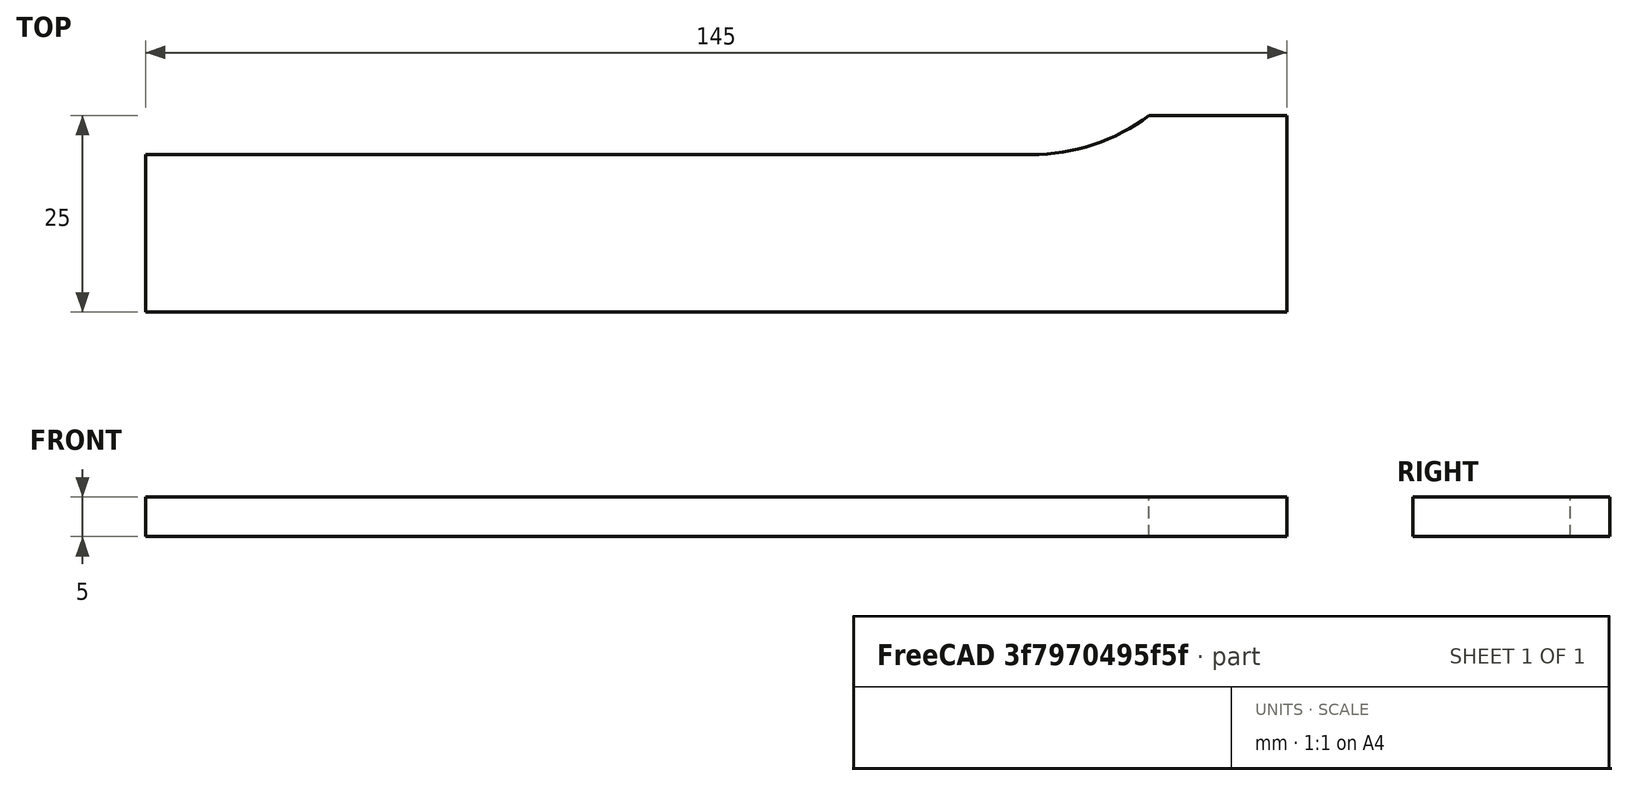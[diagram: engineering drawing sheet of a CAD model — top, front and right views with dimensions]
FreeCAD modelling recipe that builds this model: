
FCSTD DOCUMENT  (FreeCAD 0.19R)
Label: E8_40mm_Short
License: All rights reserved
LicenseURL: http://en.wikipedia.org/wiki/All_rights_reserved
objects: Sketcher::SketchObject×1, PartDesign::Pad×1, PartDesign::Body×1
note: 4 computed .brp shape members not serialized (recipe doc carries the construction recipe); baked Part::Feature solids carry a one-line shape summary decoded from their .brp

FEATURE [Sketcher::SketchObject] Sketch
  FullyConstrained = true
  MapMode = 5
  Support = -> [XY_Plane]
  sketch-geometry (6):
    g0: LineSegment StartX=127.5 StartY=25 StartZ=0 EndX=145 EndY=25 EndZ=0
    g1: LineSegment StartX=145 StartY=25 StartZ=0 EndX=145 EndY=0 EndZ=0
    g2: LineSegment StartX=145 StartY=0 StartZ=0 EndX=0 EndY=0 EndZ=0
    g3: LineSegment StartX=0 StartY=0 StartZ=0 EndX=0 EndY=20 EndZ=0
    g4: LineSegment StartX=0 StartY=20 StartZ=0 EndX=112.5 EndY=20 EndZ=0
    g5: ArcOfCircle CenterX=112.5 CenterY=45 CenterZ=0 NormalX=0 NormalY=0 NormalZ=1 AngleXU=0 Radius=25 StartAngle=4.71239 EndAngle=5.35589
  constraints (17):
    c: Horizontal(g0)
    c: PointOnObject(g1,g-1)
    c: Vertical(g1)
    c: Coincident(g2,g-1)
    c: Coincident(g2,g1)
    c: Coincident(g0,g1)
    c: Vertical(g3)
    c: Horizontal(g4)
    c: Coincident(g3,g4)
    c: Coincident(g3,g2)
    c: DistanceY(g3,g3) = 20
    c: DistanceY(g1,g1) = 25
    c: Tangent(g4,g5) = -1.5708
    c: Radius(g5) = 25
    c: Coincident(g5,g0)
    c: DistanceX(g4,g4) = 112.5
    c: DistanceX(g2,g2) = 145
FEATURE [PartDesign::Pad] Pad
  Direction = (1,1,1)
  Length = 5
  Length2 = 100
  Profile = -> Sketch
  Type = 0
FEATURE [PartDesign::Body] Body
  Group = -> [Sketch,Pad]
  Origin = -> Origin
  Tip = -> Pad
